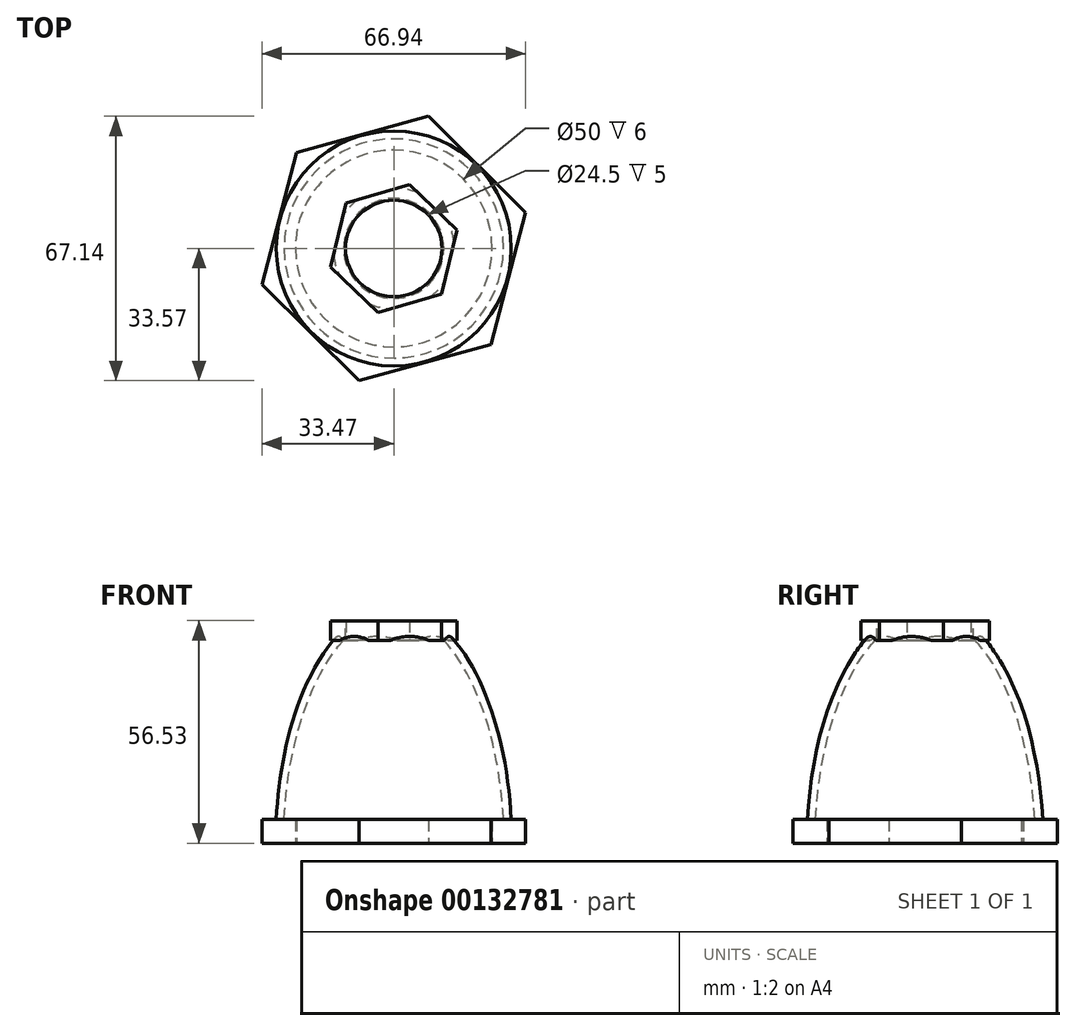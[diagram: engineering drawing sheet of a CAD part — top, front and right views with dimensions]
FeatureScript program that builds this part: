
annotation { "Feature Type Name" : "Feature", "Feature Type Description" : "" }
export const myFeature = defineFeature(function(context is Context, id is Id, definition is map)
    precondition{}
    {
        {
            var Q0;
            Q0=qCreatedBy(makeId("Front.planeOp"),FACE);
            var sketch = newSketch(context, id + "F0", { "sketchPlane" : qUnion([Q0])});
            skEllipticalArc(sketch, "E0", {});
            skLineSegment(sketch, "E1", {"start": v(0, 52.53) * mm, "end": v(14.5, 52.53) * mm});
            skLineSegment(sketch, "E2", {"start": v(0, 0) * mm, "end": v(30, 0) * mm});
            skLineSegment(sketch, "E3", {"start": v(0, 52.53) * mm, "end": v(0, 0) * mm});
            skPoint(sketch, "E4.orphan", {"position": v(-14.5, 52.53) * mm});
            skPoint(sketch, "E5.orphan", {"position": v(-30, 0) * mm});
            const initialGuessF0  = {"E0": [0, 0, 0, 1, 0.06, 0.03, 4.71238898038469, 5.778726954653852]};
            skSetInitialGuess(sketch, initialGuessF0);
            skSolve(sketch);
        }
        {
            var Q0;
            Q0 = qSketchRegion(id + "F0", true);
            var Q1;
            Q1=makeQuery(id+"F0.imprint","IMPRINT",FACE,{"disambiguationData":[TD([[makeQuery(id+"F0.imprint","IMPRINT",EDGE,{"derivedFrom":sQuery(id+"F0.wireOp",EDGE,"E0")}),1.0]])]});
            var Q2;
            Q2=sQuery(id+"F0.wireOp",EDGE,"E3");
            revolve(context, id + "F1", {"entities" : qUnion([Q0, Q1]), "axis" : qUnion([Q2]), "revolveType" : RevolveType.FULL});
        }
        {
            var Q0;
            Q0=makeQuery(id+"F1.opRevolve","SWEPT_FACE",FACE,{"disambiguationData":[OSD([sQuery(id+"F0.wireOp",EDGE,"E2")])]});
            var Q1;
            Q1=makeQuery(id+"F1.opRevolve","SWEPT_FACE",FACE,{"disambiguationData":[OSD([sQuery(id+"F0.wireOp",EDGE,"E1")])]});
            shell(context, id + "F2", {"entities" : qUnion([Q0, Q1]), "thickness" : 2 * mm});
        }
        {
            var Q0;
            Q0=qCreatedBy(makeId("Top.planeOp"),FACE);
            var sketch = newSketch(context, id + "F3", { "sketchPlane" : qUnion([Q0])});
            skCircle(sketch, "E6.cCircle", {"center": v(0, 0) * mm, "radius": 30.05 * mm, "construction": true});
            skLineSegment(sketch, "E6.0", {"start": v(24.68, -24.4) * mm, "end": v(-8.8, -33.57) * mm});
            skLineSegment(sketch, "E6.1", {"start": v(-8.8, -33.57) * mm, "end": v(-33.47, -9.17) * mm});
            skLineSegment(sketch, "E6.2", {"start": v(-33.47, -9.17) * mm, "end": v(-24.68, 24.4) * mm});
            skLineSegment(sketch, "E6.3", {"start": v(-24.68, 24.4) * mm, "end": v(8.8, 33.57) * mm});
            skLineSegment(sketch, "E6.4", {"start": v(8.8, 33.57) * mm, "end": v(33.47, 9.17) * mm});
            skLineSegment(sketch, "E6.5", {"start": v(33.47, 9.17) * mm, "end": v(24.68, -24.4) * mm});
            skPoint(sketch, "E6.0.midPoint", {"position": v(7.94, -28.99) * mm});
            skSolve(sketch);
        }
        {
            var Q0;
            Q0 = qSketchRegion(id + "F3", true);
            extrude(context, id + "F4", {"entities" : qUnion([Q0]), "operationType" : NewBodyOperationType.ADD, "depth" : 6 * mm});
        }
        {
            var Q0;
            Q0 = qSketchRegion(id + "F3", true);
            extrude(context, id + "F5", {"entities" : qUnion([Q0]), "operationType" : NewBodyOperationType.ADD, "depth" : 4 * mm});
        }
        {
            var Q0;
            Q0=qCreatedBy(makeId("Top.planeOp"),FACE);
            var sketch = newSketch(context, id + "F6", { "sketchPlane" : qUnion([Q0])});
            skCircle(sketch, "E7", {"center": v(0, 0) * mm, "radius": 25 * mm});
            skSolve(sketch);
        }
        {
            var Q0;
            Q0 = qSketchRegion(id + "F6", true);
            extrude(context, id + "F7", {"entities" : qUnion([Q0]), "operationType" : NewBodyOperationType.REMOVE, "depth" : 6 * mm});
        }
        {
            var Q0;
            Q0=makeQuery(id+"F1.opRevolve","SWEPT_FACE",FACE,{"disambiguationData":[OSD([sQuery(id+"F0.wireOp",EDGE,"E1")])]});
            var sketch = newSketch(context, id + "F8", { "sketchPlane" : qUnion([Q0])});
            skCircle(sketch, "E8.cCircle", {"center": v(0, 0) * mm, "radius": 14.5 * mm, "construction": true});
            skLineSegment(sketch, "E8.0", {"start": v(16.08, 4.66) * mm, "end": v(12.08, -11.6) * mm});
            skLineSegment(sketch, "E8.1", {"start": v(12.08, -11.6) * mm, "end": v(-4, -16.26) * mm});
            skLineSegment(sketch, "E8.2", {"start": v(-4, -16.26) * mm, "end": v(-16.08, -4.66) * mm});
            skLineSegment(sketch, "E8.3", {"start": v(-16.08, -4.66) * mm, "end": v(-12.08, 11.6) * mm});
            skLineSegment(sketch, "E8.4", {"start": v(-12.08, 11.6) * mm, "end": v(4, 16.26) * mm});
            skLineSegment(sketch, "E8.5", {"start": v(4, 16.26) * mm, "end": v(16.08, 4.66) * mm});
            skPoint(sketch, "E8.0.midPoint", {"position": v(14.08, -3.47) * mm});
            skSolve(sketch);
        }
        {
            var Q0;
            Q0 = qSketchRegion(id + "F8", true);
            extrude(context, id + "F9", {"entities" : qUnion([Q0]), "operationType" : NewBodyOperationType.ADD, "depth" : 4 * mm});
        }
        {
            var Q0;
            Q0=makeQuery(id+"F9.opExtrude","CAP_FACE",FACE,{"disambiguationData":[OSD([sQuery(id+"F8.wireOp",EDGE,"E8.0"),sQuery(id+"F8.wireOp",EDGE,"E8.1"),sQuery(id+"F8.wireOp",EDGE,"E8.2"),sQuery(id+"F8.wireOp",EDGE,"E8.3"),sQuery(id+"F8.wireOp",EDGE,"E8.4"),sQuery(id+"F8.wireOp",EDGE,"E8.5")])],"isStart":false});
            var sketch = newSketch(context, id + "F10", { "sketchPlane" : qUnion([Q0])});
            skCircle(sketch, "E9.cCircle", {"center": v(0, 0) * mm, "radius": 14.5 * mm, "construction": true});
            skLineSegment(sketch, "E9.0", {"start": v(-12.08, 11.6) * mm, "end": v(4, 16.26) * mm});
            skLineSegment(sketch, "E9.1", {"start": v(4, 16.26) * mm, "end": v(16.08, 4.66) * mm});
            skLineSegment(sketch, "E9.2", {"start": v(16.08, 4.66) * mm, "end": v(12.08, -11.6) * mm});
            skLineSegment(sketch, "E9.3", {"start": v(12.08, -11.6) * mm, "end": v(-4, -16.26) * mm});
            skLineSegment(sketch, "E9.4", {"start": v(-4, -16.26) * mm, "end": v(-16.08, -4.66) * mm});
            skLineSegment(sketch, "E9.5", {"start": v(-16.08, -4.66) * mm, "end": v(-12.08, 11.6) * mm});
            skPoint(sketch, "E9.0.midPoint", {"position": v(-4.04, 13.93) * mm});
            skSolve(sketch);
        }
        {
            var Q0;
            Q0 = qSketchRegion(id + "F10", true);
            extrude(context, id + "F11", {"entities" : qUnion([Q0]), "operationType" : NewBodyOperationType.ADD, "oppositeDirection" : true, "depth" : 5 * mm});
        }
        {
            var Q0;
            Q0=makeQuery(id+"F9.opExtrude","CAP_FACE",FACE,{"disambiguationData":[OSD([sQuery(id+"F8.wireOp",EDGE,"E8.0"),sQuery(id+"F8.wireOp",EDGE,"E8.1"),sQuery(id+"F8.wireOp",EDGE,"E8.2"),sQuery(id+"F8.wireOp",EDGE,"E8.3"),sQuery(id+"F8.wireOp",EDGE,"E8.4"),sQuery(id+"F8.wireOp",EDGE,"E8.5")])],"isStart":false});
            var sketch = newSketch(context, id + "F12", { "sketchPlane" : qUnion([Q0])});
            skCircle(sketch, "E10", {"center": v(0, 0) * mm, "radius": 12.25 * mm});
            skSolve(sketch);
        }
        {
            var Q0;
            Q0 = qSketchRegion(id + "F12", true);
            extrude(context, id + "F13", {"entities" : qUnion([Q0]), "operationType" : NewBodyOperationType.REMOVE, "oppositeDirection" : true, "depth" : 25 * mm});
        }
    });
